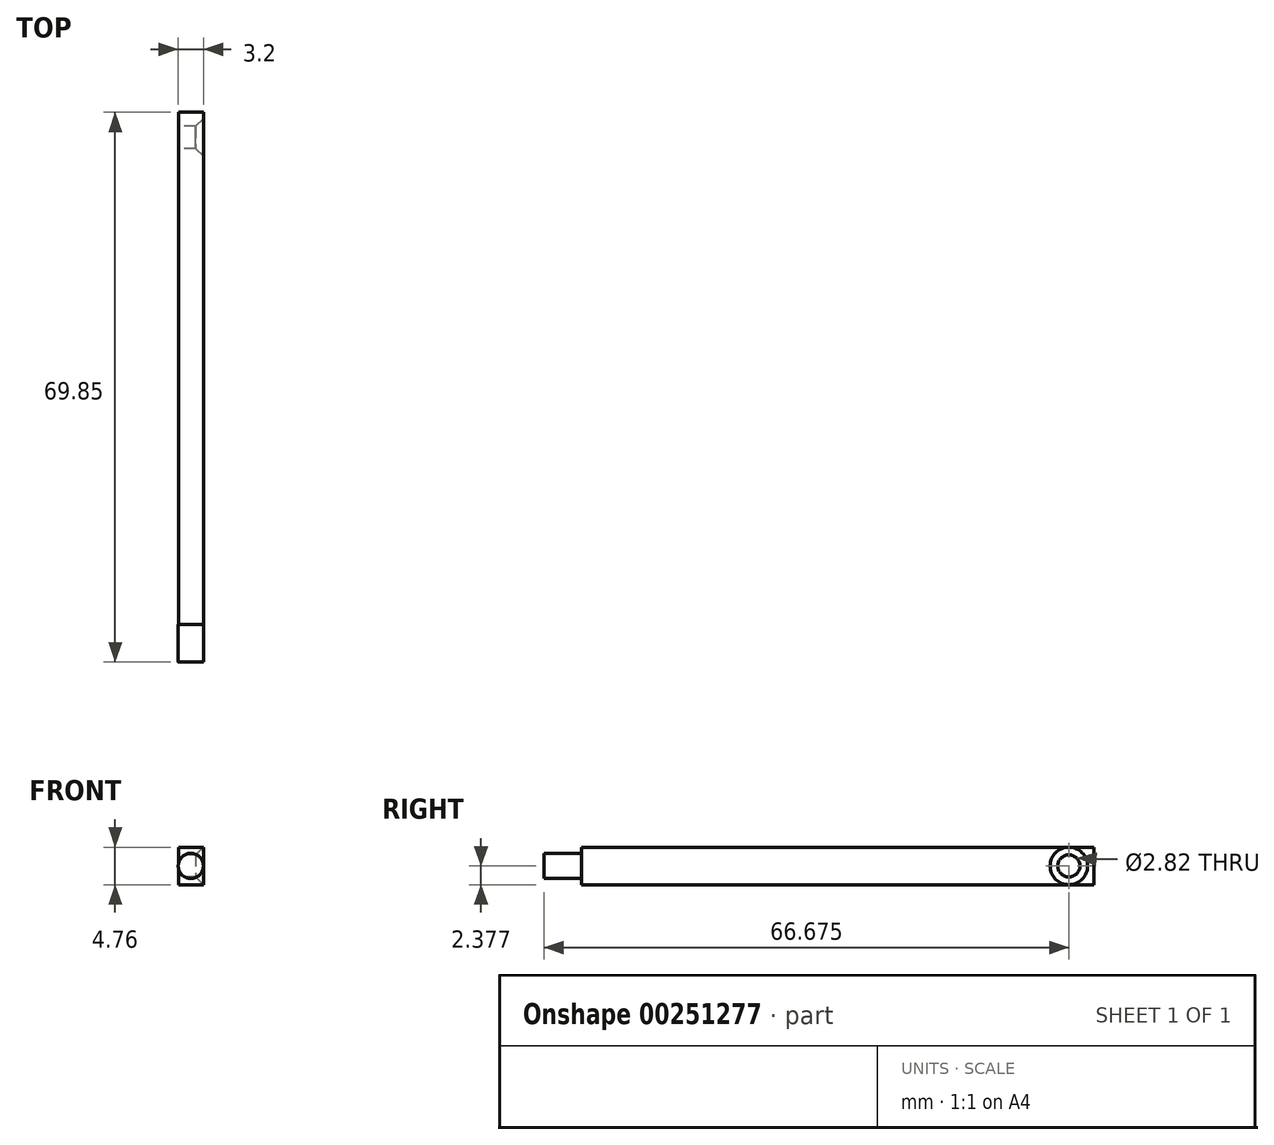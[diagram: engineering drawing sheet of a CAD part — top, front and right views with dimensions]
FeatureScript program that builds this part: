
annotation { "Feature Type Name" : "Feature", "Feature Type Description" : "" }
export const myFeature = defineFeature(function(context is Context, id is Id, definition is map)
    precondition{}
    {
        {
            var Q0;
            Q0=qCreatedBy(makeId("Front.planeOp"),FACE);
            var sketch = newSketch(context, id + "F0", { "sketchPlane" : qUnion([Q0])});
            skLineSegment(sketch, "E0.bottom", {"start": v(23.62, 20.3) * mm, "end": v(26.8, 20.3) * mm});
            skLineSegment(sketch, "E0.top", {"start": v(23.62, 15.54) * mm, "end": v(26.8, 15.54) * mm});
            skLineSegment(sketch, "E0.left", {"start": v(23.62, 20.3) * mm, "end": v(23.62, 15.54) * mm});
            skLineSegment(sketch, "E0.right", {"start": v(26.8, 20.3) * mm, "end": v(26.8, 15.54) * mm});
            skSolve(sketch);
        }
        {
            var Q0;
            Q0 = qSketchRegion(id + "F0", true);
            extrude(context, id + "F1", {"entities" : qUnion([Q0]), "depth" : 65.1 * mm});
        }
        {
            var Q0;
            Q0=makeQuery(id+"F1.opExtrude","CAP_FACE",FACE,{"disambiguationData":[OSD([sQuery(id+"F0.wireOp",EDGE,"E0.bottom"),sQuery(id+"F0.wireOp",EDGE,"E0.top"),sQuery(id+"F0.wireOp",EDGE,"E0.left"),sQuery(id+"F0.wireOp",EDGE,"E0.right")])],"isStart":false});
            var sketch = newSketch(context, id + "F2", { "sketchPlane" : qUnion([Q0])});
            skCircle(sketch, "E1", {"center": v(25.21, 17.92) * mm, "radius": 1.6 * mm});
            skSolve(sketch);
        }
        {
            var Q0;
            Q0 = qSketchRegion(id + "F2", true);
            extrude(context, id + "F3", {"entities" : qUnion([Q0]), "operationType" : NewBodyOperationType.ADD, "depth" : 4.76 * mm});
        }
        {
            var Q0;
            Q0=makeQuery(id+"F1.opExtrude","SWEPT_FACE",FACE,{"disambiguationData":[OSD([sQuery(id+"F0.wireOp",EDGE,"E0.right")])]});
            var sketch = newSketch(context, id + "F4", { "sketchPlane" : qUnion([Q0])});
            skPoint(sketch, "E2", {"position": v(-3.18, 17.92) * mm});
            skSolve(sketch);
        }
        {
            var Q0;
            Q0=sQuery(id+"F4.wireOp",VERTEX,"E2");
            var Q1;
            Q1=makeQuery(id+"F1.opExtrude","SWEPT_BODY",BODY,{"disambiguationData":[OSD([sQuery(id+"F0.wireOp",EDGE,"E0.bottom"),sQuery(id+"F0.wireOp",EDGE,"E0.top"),sQuery(id+"F0.wireOp",EDGE,"E0.left"),sQuery(id+"F0.wireOp",EDGE,"E0.right")])]});
            hole(context, id + "F5", {"style" : HoleStyle.C_SINK, "endStyle" : HoleEndStyle.THROUGH, "holeDiameter" : 2.82 * mm, "cSinkDiameter" : 4.76 * mm, "cSinkAngle" : 90 * degree, "tappedDepth" : 12.7 * mm, "tapClearance" : 3, "locations" : qUnion([Q0]), "scope" : qUnion([Q1]), "startStyle" : HoleStartStyle.PART});
        }
    });
